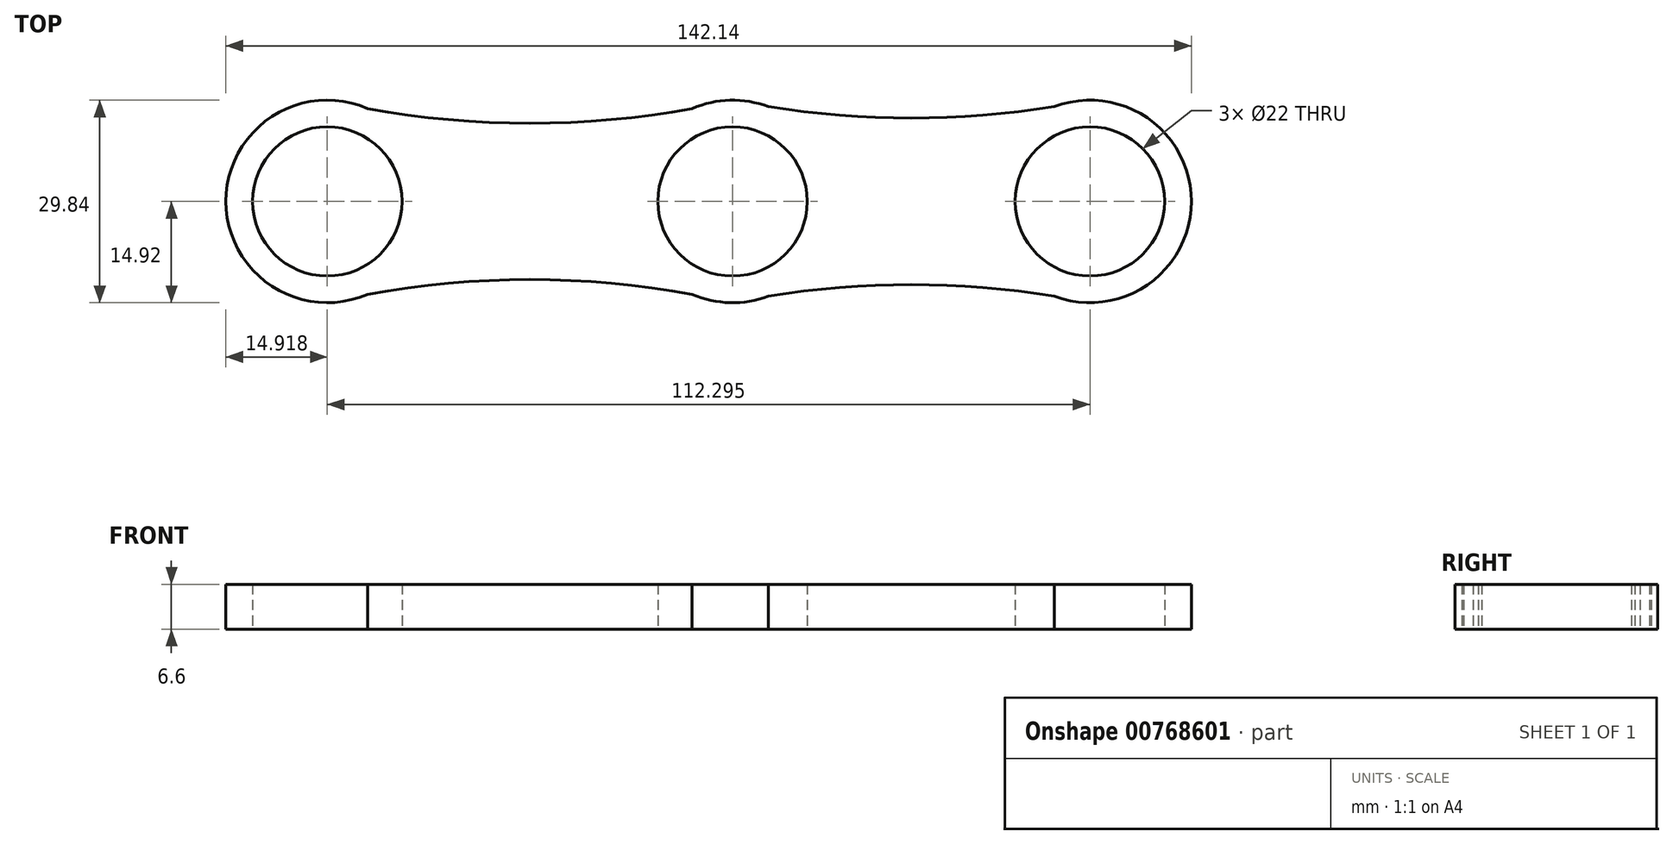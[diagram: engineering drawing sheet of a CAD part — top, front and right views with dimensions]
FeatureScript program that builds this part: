
annotation { "Feature Type Name" : "Feature", "Feature Type Description" : "" }
export const myFeature = defineFeature(function(context is Context, id is Id, definition is map)
    precondition{}
    {
        {
            var Q0;
            Q0=qCreatedBy(makeId("Top.planeOp"),FACE);
            var sketch = newSketch(context, id + "F0", { "sketchPlane" : qUnion([Q0])});
            skCircle(sketch, "E0", {"center": v(0, 0) * mm, "radius": 11 * mm});
            skCircle(sketch, "E1", {"center": v(0, 0) * mm, "radius": 14.92 * mm});
            skCircle(sketch, "E2", {"center": v(-59.67, 0) * mm, "radius": 14.92 * mm});
            skCircle(sketch, "E3", {"center": v(-59.67, 0) * mm, "radius": 11 * mm});
            skCircle(sketch, "E4", {"center": v(52.62, 0) * mm, "radius": 11 * mm});
            skCircle(sketch, "E5", {"center": v(52.62, 0) * mm, "radius": 14.92 * mm});
            skArc(sketch, "E6", {"start": v(52.62, -14.92) * mm, "mid": v(26.31, -12.28) * mm, "end": v(0, -14.92) * mm});
            skArc(sketch, "E7", {"start": v(0, 14.92) * mm, "mid": v(26.31, 12.28) * mm, "end": v(52.62, 14.92) * mm});
            skArc(sketch, "E8", {"start": v(-59.67, 14.92) * mm, "mid": v(-29.84, 11.5) * mm, "end": v(0, 14.92) * mm});
            skArc(sketch, "E9", {"start": v(0, -14.92) * mm, "mid": v(-29.84, -11.5) * mm, "end": v(-59.67, -14.92) * mm});
            skSolve(sketch);
        }
        {
            var Q0;
            Q0 = qSketchRegion(id + "F0", true);
            extrude(context, id + "F1", {"entities" : qUnion([Q0]), "depth" : 6.6 * mm, "offsetDistance" : 25 * mm});
        }
    });
